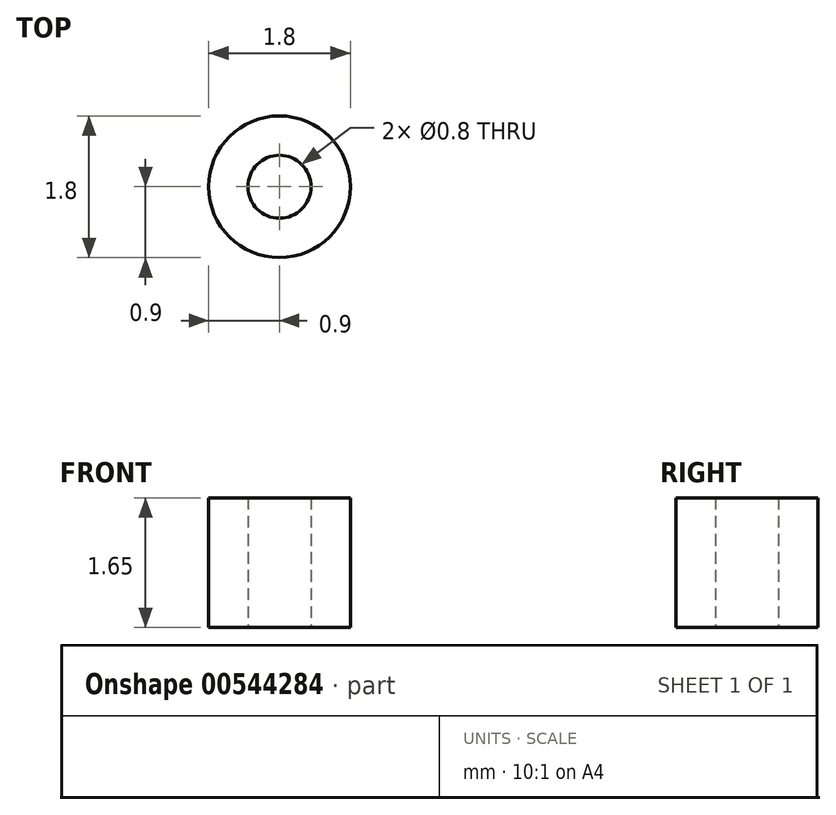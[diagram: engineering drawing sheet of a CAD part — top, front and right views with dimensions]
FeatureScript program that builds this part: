
annotation { "Feature Type Name" : "Feature", "Feature Type Description" : "" }
export const myFeature = defineFeature(function(context is Context, id is Id, definition is map)
    precondition{}
    {
        {
            var Q0;
            Q0=qCreatedBy(makeId("Top.planeOp"),FACE);
            var sketch = newSketch(context, id + "F0", { "sketchPlane" : qUnion([Q0])});
            skCircle(sketch, "E0", {"center": v(0, 0) * mm, "radius": 0.9 * mm});
            skCircle(sketch, "E1", {"center": v(0, 0) * mm, "radius": 0.4 * mm});
            skSolve(sketch);
        }
        {
            var Q0;
            Q0=qSketchRegion(id+"F0",true);
            extrude(context, id + "F1", {"entities" : qUnion([Q0]), "depth" : 1.65 * mm});
        }
    });
